# Revit family: 1.5(2.2,2.8,3.6)kW
name_source: partatom
category: Mechanical Equipment
revit_build: Autodesk Revit 2013 (Build: 20120221_2030(x64)
units: mm (PartAtom-declared; Revit-internal decimal feet)

## types (4) — shared parameters
Condensation = air
Depth = 265 mm  [stored 0.869423 ft]
Description = High efficiency air cooled
Gas = R410a/R32
Gas pipe = 12.7 mm  [stored 0.0416667 ft]
Height = 295 mm  [stored 0.967848 ft]
Installation = Indoor installation
Liquid pipe = 6.35 mm  [stored 0.0208333 ft]
Machine material = Galvanized Steel
Maximum Fuse Amps = 15 A
Minimum Circuit Amps = 0 A
Panel color = Polar white
Power supply = 220-240V, 50Hz
Series = VRF IDU
Width = 750 mm  [stored 2.46063 ft]
clearance access left = 50 mm  [stored 0.164042 ft]
clearance access right = 50 mm  [stored 0.164042 ft]

## per-type parameters (varying)
| type | Air  Flow | Cooling Capacity | Cooling Power Input | Heating Capacity | Heating Power Input | Net Weight |
| 1.5kW | 460/440/420/400/380/360/340 m3/h | 1500 W | 18 W | 1700 W | 18 W | 9.00 kg |
| 2.2kW | 500/470/440/410/390/370/340 m3/h | 2200 W | 21 W | 2400 W | 21 W | 9.00 kg |
| 2.8kW | 540/510/470/430/400/370/340 m3/h | 2800 W | 24 W | 3200 W | 24 W | 10.00 kg |
| 3.6kW | 580/540/500/460/420/380/340 m3/h | 3600 W | 27 W | 4000 W | 27 W | 10.00 kg |

note: column(s) folded — value = type name in every type: Model

note: [stored X ft] marks values corroborated as IEEE doubles in the binary element streams (Revit-internal decimal feet)

## geometry (parser evidence)
native form markers: Sweep x1
no freeform markers — native parametric forms only
